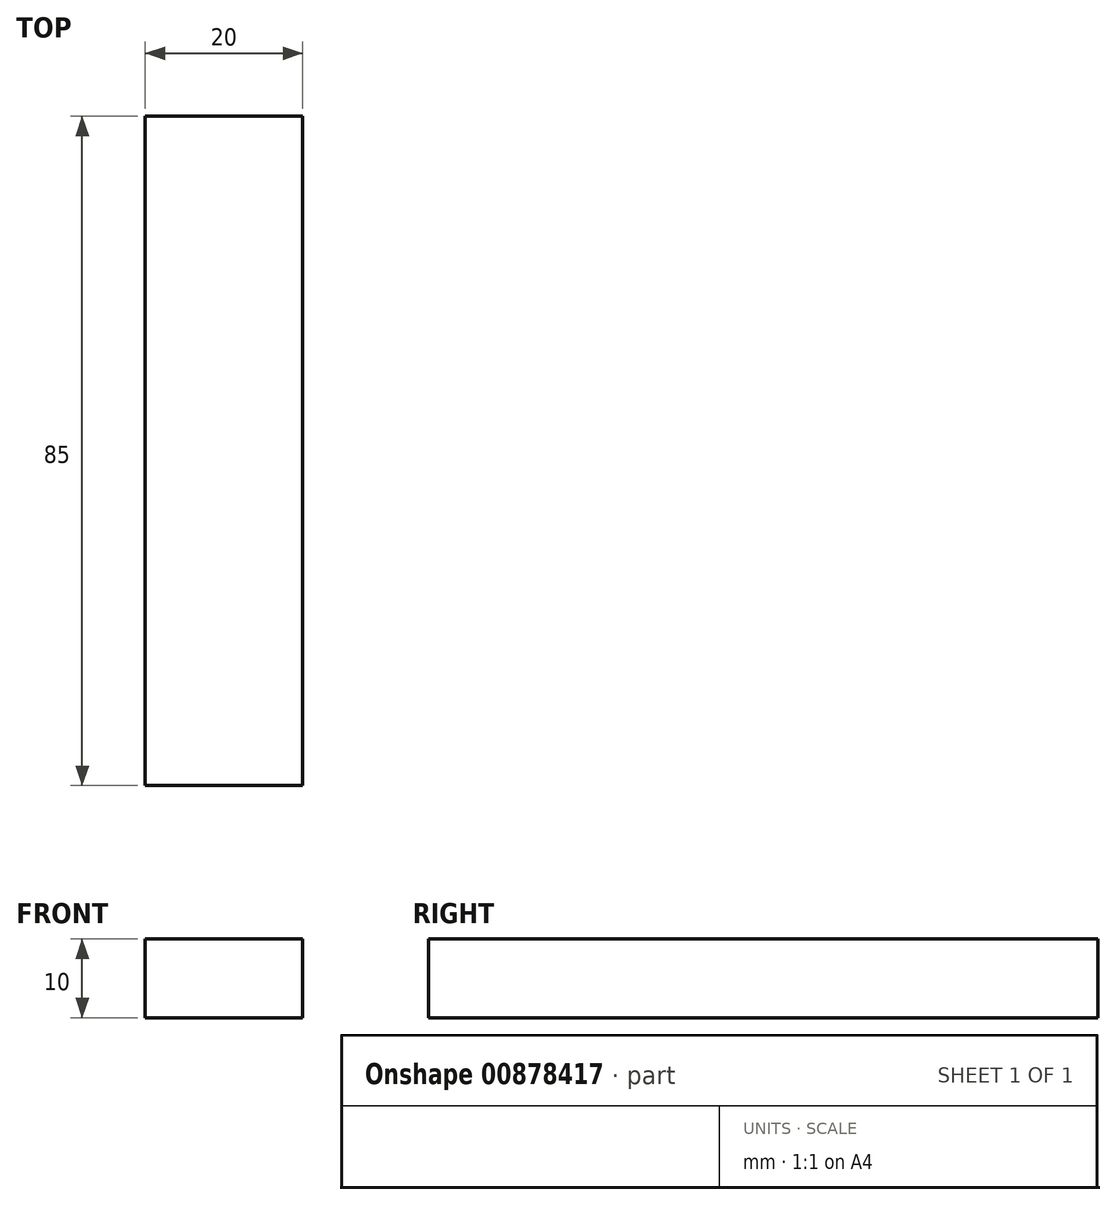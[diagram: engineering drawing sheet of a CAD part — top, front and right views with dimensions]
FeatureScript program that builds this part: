
annotation { "Feature Type Name" : "Feature", "Feature Type Description" : "" }
export const myFeature = defineFeature(function(context is Context, id is Id, definition is map)
    precondition{}
    {
        {
            var Q0;
            Q0=qCreatedBy(makeId("Top.planeOp"),FACE);
            var sketch = newSketch(context, id + "F0", { "sketchPlane" : qUnion([Q0])});
            skLineSegment(sketch, "E0.bottom", {"start": v(1.2, -9.5) * mm, "end": v(21.2, -9.5) * mm});
            skLineSegment(sketch, "E0.top", {"start": v(1.2, 75.5) * mm, "end": v(21.2, 75.5) * mm});
            skLineSegment(sketch, "E0.left", {"start": v(1.2, -9.5) * mm, "end": v(1.2, 75.5) * mm});
            skLineSegment(sketch, "E0.right", {"start": v(21.2, -9.5) * mm, "end": v(21.2, 75.5) * mm});
            skSolve(sketch);
        }
        {
            var Q0;
            Q0=makeQuery(id+"F0.imprint","IMPRINT",FACE,{"disambiguationData":[TD([[makeQuery(id+"F0.imprint","IMPRINT",EDGE,{"derivedFrom":sQuery(id+"F0.wireOp",EDGE,"E0.bottom")}),1.0]])]});
            extrude(context, id + "F1", {"entities" : qUnion([Q0]), "depth" : 10 * mm, "offsetDistance" : 25 * mm});
        }
    });
